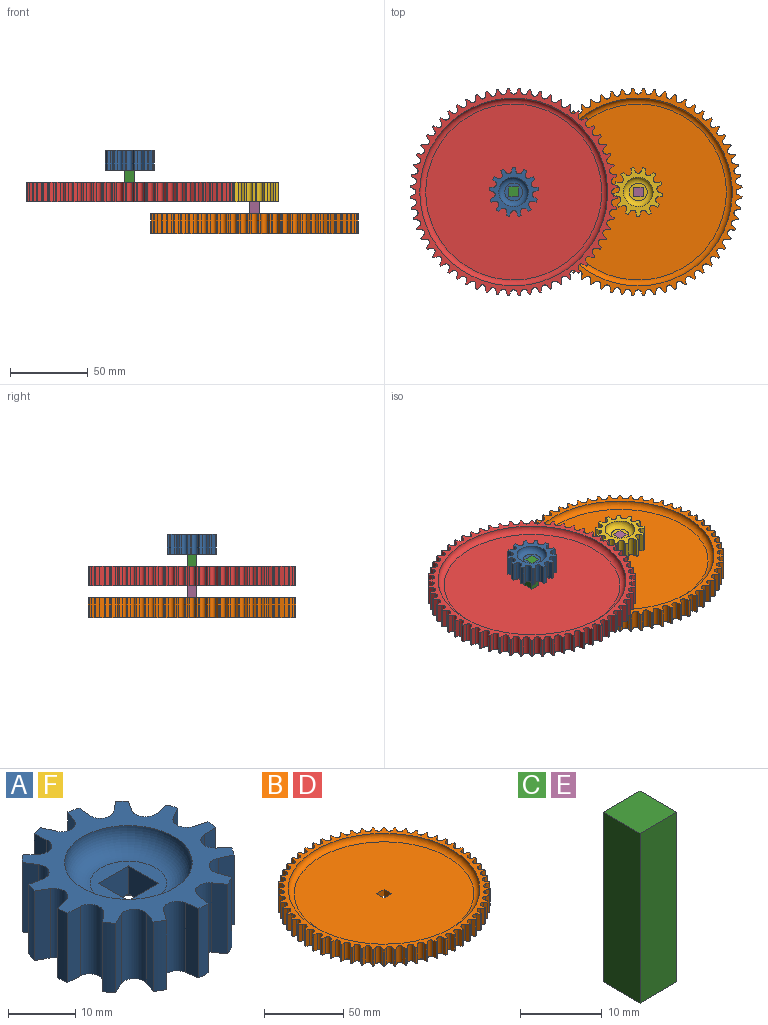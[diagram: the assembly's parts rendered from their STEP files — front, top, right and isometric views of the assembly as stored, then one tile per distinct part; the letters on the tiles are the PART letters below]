
ASSEMBLY  parts=6 mates=5
PART A: 62 faces, bbox 31.7x31.5x15.4 mm
  f0: cylinder r=15.88mm len=12.7mm, axis (0,0,-1), area 24.5mm2, adj f2,f7,f49,f50
  f1: cylinder r=2.06mm len=12.7mm, axis (0,0,-1), area 61.6mm2, adj f2,f3,f49,f50
  f2: plane 12.7x1.9mm, normal (-0.64,0.77,0), area 31.4mm2, adj f0,f1,f49,f50
  f3: plane 12.7x2.46mm, normal (1,-0.09,0), area 31.4mm2, adj f1,f48,f49,f50
  f4: cylinder r=15.88mm len=12.7mm, axis (0,0,-1), area 24.5mm2, adj f6,f11,f49,f50
  f5: cylinder r=2.06mm len=12.7mm, axis (0,0,-1), area 61.6mm2, adj f6,f7,f49,f50
  f6: plane 12.7x2.42mm, normal (-0.21,0.98,0), area 31.4mm2, adj f4,f5,f49,f50
  f7: plane 12.7x2.08mm, normal (0.84,-0.54,0), area 31.4mm2, adj f0,f5,f49,f50
  f8: cylinder r=15.88mm len=12.7mm, axis (0,0,-1), area 24.5mm2, adj f10,f15,f49,f50
  f9: cylinder r=2.06mm len=12.7mm, axis (0,0,-1), area 61.6mm2, adj f10,f11,f49,f50
  f10: plane 12.7x2.38mm, normal (0.27,0.96,0), area 31.4mm2, adj f8,f9,f49,f50
  f11: plane 12.7x2.15mm, normal (0.49,-0.87,0), area 31.4mm2, adj f4,f9,f49,f50
  f12: cylinder r=15.88mm len=12.7mm, axis (0,0,-1), area 24.5mm2, adj f14,f19,f49,f50
  f13: cylinder r=2.06mm len=12.7mm, axis (0,0,-1), area 61.6mm2, adj f14,f15,f49,f50
  f14: plane 12.7x1.8mm, normal (0.69,0.73,0), area 31.4mm2, adj f12,f13,f49,f50
  f15: plane 12.7x2.47mm, normal (0.03,-1,0), area 31.4mm2, adj f8,f13,f49,f50
  f16: cylinder r=15.88mm len=12.7mm, axis (0,0,-1), area 24.5mm2, adj f18,f23,f49,f50
  f17: cylinder r=2.06mm len=12.7mm, axis (0,0,-1), area 61.6mm2, adj f18,f19,f49,f50
  f18: plane 12.7x2.34mm, normal (0.95,0.32,0), area 31.4mm2, adj f16,f17,f49,f50
  f19: plane 12.7x2.22mm, normal (-0.44,-0.9,0), area 31.4mm2, adj f12,f17,f49,f50
  f20: cylinder r=15.88mm len=12.7mm, axis (0,0,-1), area 24.5mm2, adj f22,f27,f49,f50
  f21: cylinder r=2.06mm len=12.7mm, axis (0,0,-1), area 61.6mm2, adj f22,f23,f49,f50
  f22: plane 12.7x2.44mm, normal (0.99,-0.15,0), area 31.4mm2, adj f20,f21,f49,f50
  f23: plane 12.7x1.99mm, normal (-0.8,-0.59,0), area 31.4mm2, adj f16,f21,f49,f50
  f24: cylinder r=15.88mm len=12.7mm, axis (0,0,-1), area 24.5mm2, adj f26,f31,f49,f50
  f25: cylinder r=2.06mm len=12.7mm, axis (0,0,-1), area 61.6mm2, adj f26,f27,f49,f50
  f26: plane 12.7x1.99mm, normal (0.8,-0.59,0), area 31.4mm2, adj f24,f25,f49,f50
  f27: plane 12.7x2.44mm, normal (-0.99,-0.15,0), area 31.4mm2, adj f20,f25,f49,f50
  f28: cylinder r=15.88mm len=12.7mm, axis (0,0,-1), area 24.5mm2, adj f30,f35,f49,f50
  f29: cylinder r=2.06mm len=12.7mm, axis (0,0,-1), area 61.6mm2, adj f30,f31,f49,f50
  f30: plane 12.7x2.22mm, normal (0.44,-0.9,0), area 31.4mm2, adj f28,f29,f49,f50
  f31: plane 12.7x2.34mm, normal (-0.95,0.32,0), area 31.4mm2, adj f24,f29,f49,f50
  f32: cylinder r=15.88mm len=12.7mm, axis (0,0,-1), area 24.5mm2, adj f34,f39,f49,f50
  f33: cylinder r=2.06mm len=12.7mm, axis (0,0,-1), area 61.6mm2, adj f34,f35,f49,f50
  f34: plane 12.7x2.47mm, normal (-0.03,-1,0), area 31.4mm2, adj f32,f33,f49,f50
  f35: plane 12.7x1.8mm, normal (-0.69,0.73,0), area 31.4mm2, adj f28,f33,f49,f50
  f36: cylinder r=15.88mm len=12.7mm, axis (0,0,-1), area 24.5mm2, adj f38,f43,f49,f50
  f37: cylinder r=2.06mm len=12.7mm, axis (0,0,-1), area 61.6mm2, adj f38,f39,f49,f50
  f38: plane 12.7x2.15mm, normal (-0.49,-0.87,0), area 31.4mm2, adj f36,f37,f49,f50
  f39: plane 12.7x2.38mm, normal (-0.27,0.96,0), area 31.4mm2, adj f32,f37,f49,f50
  f40: cylinder r=15.88mm len=12.7mm, axis (0,0,-1), area 24.5mm2, adj f42,f47,f49,f50
  f41: cylinder r=2.06mm len=12.7mm, axis (0,0,-1), area 61.6mm2, adj f42,f43,f49,f50
  f42: plane 12.7x2.08mm, normal (-0.84,-0.54,0), area 31.4mm2, adj f40,f41,f49,f50
  f43: plane 12.7x2.42mm, normal (0.21,0.98,0), area 31.4mm2, adj f36,f41,f49,f50
  f44: cylinder r=15.88mm len=12.7mm, axis (0,0,-1), area 24.5mm2, adj f46,f49,f50,f57
  f45: cylinder r=2.06mm len=12.7mm, axis (0,0,-1), area 61.6mm2, adj f46,f47,f49,f50
  f46: plane 12.7x2.46mm, normal (-1,-0.09,0), area 31.4mm2, adj f44,f45,f49,f50
  f47: plane 12.7x1.9mm, normal (0.64,0.77,0), area 31.4mm2, adj f40,f45,f49,f50
  f48: cylinder r=15.88mm len=12.7mm, axis (0,0,-1), area 24.5mm2, adj f3,f49,f50,f56
  f49: plane 31.69x31.49mm, normal (0,0,-1), area 307.2mm2, adj f0,f1,f2,f3,f4,f5,f6,f7
  f50: plane 31.69x31.49mm, normal (0,0,1), area 307.2mm2, adj f0,f1,f2,f3,f4,f5,f6,f7
  f51: torus R=5.71mm, axis (0,0,-1), area 306.1mm2, adj f49,f54
  f52: torus R=5.71mm, axis (0,0,-1), area 306.1mm2, adj f50,f53
  f53: plane 11.43x11.43mm, normal (0,0,1), area 62.3mm2, adj f52,f58,f59,f60,f61
  f54: plane 11.43x11.43mm, normal (0,0,-1), area 62.3mm2, adj f51,f58,f59,f60,f61
  f55: cylinder r=2.06mm len=12.7mm, axis (0,0,-1), area 61.6mm2, adj f49,f50,f56,f57
  f56: plane 12.7x2.28mm, normal (-0.92,0.38,0), area 31.4mm2, adj f48,f49,f50,f55
  f57: plane 12.7x2.28mm, normal (0.92,0.38,0), area 31.4mm2, adj f44,f49,f50,f55
  f58: plane 6.35x5.08mm, normal (-1,0,0), area 32.3mm2, adj f53,f54,f59,f61
  f59: plane 6.35x5.08mm, normal (0,-1,0), area 32.3mm2, adj f53,f54,f58,f60
  f60: plane 6.35x5.08mm, normal (1,0,0), area 32.3mm2, adj f53,f54,f59,f61
  f61: plane 6.35x5.08mm, normal (0,1,0), area 32.3mm2, adj f53,f54,f58,f60
PART B: 250 faces, bbox 133.2x133.2x15.4 mm
  f0: plane 113.03x113.03mm, normal (0,0,1), area 9993.8mm2, adj f239,f246,f247,f248,f249
  f1: plane 113.03x113.03mm, normal (0,0,-1), area 9993.8mm2, adj f240,f246,f247,f248,f249
  f2: cylinder r=66.67mm len=12.7mm, axis (0,0,-1), area 14.1mm2, adj f4,f9,f241,f242
  f3: cylinder r=2.06mm len=12.7mm, axis (0,0,1), area 61.6mm2, adj f4,f5,f241,f242
  f4: plane 12.7x2.35mm, normal (-0.88,0.48,0), area 34.1mm2, adj f2,f3,f241,f242
  f5: plane 12.7x2.57mm, normal (0.96,0.29,0), area 34.1mm2, adj f3,f238,f241,f242
  f6: cylinder r=66.67mm len=12.7mm, axis (0,0,-1), area 14.1mm2, adj f8,f13,f241,f242
  f7: cylinder r=2.06mm len=12.7mm, axis (0,0,1), area 61.6mm2, adj f8,f9,f241,f242
  f8: plane 12.7x2.21mm, normal (-0.82,0.57,0), area 34.1mm2, adj f6,f7,f241,f242
  f9: plane 12.7x2.64mm, normal (0.98,0.18,0), area 34.1mm2, adj f2,f7,f241,f242
  f10: cylinder r=66.67mm len=12.7mm, axis (0,0,-1), area 14.1mm2, adj f12,f17,f241,f242
  f11: cylinder r=2.06mm len=12.7mm, axis (0,0,1), area 61.6mm2, adj f12,f13,f241,f242
  f12: plane 12.7x2.04mm, normal (-0.76,0.65,0), area 34.1mm2, adj f10,f11,f241,f242
  f13: plane 12.7x2.67mm, normal (1,0.08,0), area 34.1mm2, adj f6,f11,f241,f242
  f14: cylinder r=66.67mm len=12.7mm, axis (0,0,-1), area 14.1mm2, adj f16,f21,f241,f242
  f15: cylinder r=2.06mm len=12.7mm, axis (0,0,1), area 61.6mm2, adj f16,f17,f241,f242
  f16: plane 12.7x1.95mm, normal (-0.69,0.73,0), area 34.1mm2, adj f14,f15,f241,f242
  f17: plane 12.7x2.68mm, normal (1,-0.02,0), area 34.1mm2, adj f10,f15,f241,f242
  f18: cylinder r=66.67mm len=12.7mm, axis (0,0,-1), area 14.1mm2, adj f20,f25,f241,f242
  f19: cylinder r=2.06mm len=12.7mm, axis (0,0,1), area 61.6mm2, adj f20,f21,f241,f242
  f20: plane 12.7x2.13mm, normal (-0.61,0.79,0), area 34.1mm2, adj f18,f19,f241,f242
  f21: plane 12.7x2.66mm, normal (0.99,-0.13,0), area 34.1mm2, adj f14,f19,f241,f242
  f22: cylinder r=66.67mm len=12.7mm, axis (0,0,-1), area 14.1mm2, adj f24,f29,f241,f242
  f23: cylinder r=2.06mm len=12.7mm, axis (0,0,1), area 61.6mm2, adj f24,f25,f241,f242
  f24: plane 12.7x2.29mm, normal (-0.52,0.85,0), area 34.1mm2, adj f22,f23,f241,f242
  f25: plane 12.7x2.61mm, normal (0.97,-0.23,0), area 34.1mm2, adj f18,f23,f241,f242
  f26: cylinder r=66.67mm len=12.7mm, axis (0,0,-1), area 14.1mm2, adj f28,f33,f241,f242
  f27: cylinder r=2.06mm len=12.7mm, axis (0,0,1), area 61.6mm2, adj f28,f29,f241,f242
  f28: plane 12.7x2.42mm, normal (-0.43,0.9,0), area 34.1mm2, adj f26,f27,f241,f242
  f29: plane 12.7x2.53mm, normal (0.94,-0.33,0), area 34.1mm2, adj f22,f27,f241,f242
  f30: cylinder r=66.67mm len=12.7mm, axis (0,0,-1), area 14.1mm2, adj f32,f37,f241,f242
  f31: cylinder r=2.06mm len=12.7mm, axis (0,0,1), area 61.6mm2, adj f32,f33,f241,f242
  f32: plane 12.7x2.53mm, normal (-0.33,0.94,0), area 34.1mm2, adj f30,f31,f241,f242
  f33: plane 12.7x2.42mm, normal (0.9,-0.43,0), area 34.1mm2, adj f26,f31,f241,f242
  f34: cylinder r=66.67mm len=12.7mm, axis (0,0,-1), area 14.1mm2, adj f36,f41,f241,f242
  f35: cylinder r=2.06mm len=12.7mm, axis (0,0,1), area 61.6mm2, adj f36,f37,f241,f242
  f36: plane 12.7x2.61mm, normal (-0.23,0.97,0), area 34.1mm2, adj f34,f35,f241,f242
  f37: plane 12.7x2.29mm, normal (0.85,-0.52,0), area 34.1mm2, adj f30,f35,f241,f242
  f38: cylinder r=66.67mm len=12.7mm, axis (0,0,-1), area 14.1mm2, adj f40,f45,f241,f242
  f39: cylinder r=2.06mm len=12.7mm, axis (0,0,1), area 61.6mm2, adj f40,f41,f241,f242
  f40: plane 12.7x2.66mm, normal (-0.13,0.99,0), area 34.1mm2, adj f38,f39,f241,f242
  f41: plane 12.7x2.13mm, normal (0.79,-0.61,0), area 34.1mm2, adj f34,f39,f241,f242
  f42: cylinder r=66.67mm len=12.7mm, axis (0,0,-1), area 14.1mm2, adj f44,f49,f241,f242
  f43: cylinder r=2.06mm len=12.7mm, axis (0,0,1), area 61.6mm2, adj f44,f45,f241,f242
  f44: plane 12.7x2.68mm, normal (-0.02,1,0), area 34.1mm2, adj f42,f43,f241,f242
  f45: plane 12.7x1.95mm, normal (0.73,-0.69,0), area 34.1mm2, adj f38,f43,f241,f242
  f46: cylinder r=66.67mm len=12.7mm, axis (0,0,-1), area 14.1mm2, adj f48,f53,f241,f242
  f47: cylinder r=2.06mm len=12.7mm, axis (0,0,1), area 61.6mm2, adj f48,f49,f241,f242
  f48: plane 12.7x2.67mm, normal (0.08,1,0), area 34.1mm2, adj f46,f47,f241,f242
  f49: plane 12.7x2.04mm, normal (0.65,-0.76,0), area 34.1mm2, adj f42,f47,f241,f242
  f50: cylinder r=66.67mm len=12.7mm, axis (0,0,-1), area 14.1mm2, adj f52,f57,f241,f242
  f51: cylinder r=2.06mm len=12.7mm, axis (0,0,1), area 61.6mm2, adj f52,f53,f241,f242
  f52: plane 12.7x2.64mm, normal (0.18,0.98,0), area 34.1mm2, adj f50,f51,f241,f242
  f53: plane 12.7x2.21mm, normal (0.57,-0.82,0), area 34.1mm2, adj f46,f51,f241,f242
  f54: cylinder r=66.67mm len=12.7mm, axis (0,0,-1), area 14.1mm2, adj f56,f61,f241,f242
  f55: cylinder r=2.06mm len=12.7mm, axis (0,0,1), area 61.6mm2, adj f56,f57,f241,f242
  f56: plane 12.7x2.57mm, normal (0.29,0.96,0), area 34.1mm2, adj f54,f55,f241,f242
  f57: plane 12.7x2.35mm, normal (0.48,-0.88,0), area 34.1mm2, adj f50,f55,f241,f242
  f58: cylinder r=66.67mm len=12.7mm, axis (0,0,-1), area 14.1mm2, adj f60,f65,f241,f242
  f59: cylinder r=2.06mm len=12.7mm, axis (0,0,1), area 61.6mm2, adj f60,f61,f241,f242
  f60: plane 12.7x2.48mm, normal (0.38,0.92,0), area 34.1mm2, adj f58,f59,f241,f242
  f61: plane 12.7x2.48mm, normal (0.38,-0.92,0), area 34.1mm2, adj f54,f59,f241,f242
  f62: cylinder r=66.67mm len=12.7mm, axis (0,0,-1), area 14.1mm2, adj f64,f69,f241,f242
  f63: cylinder r=2.06mm len=12.7mm, axis (0,0,1), area 61.6mm2, adj f64,f65,f241,f242
  f64: plane 12.7x2.35mm, normal (0.48,0.88,0), area 34.1mm2, adj f62,f63,f241,f242
  f65: plane 12.7x2.57mm, normal (0.29,-0.96,0), area 34.1mm2, adj f58,f63,f241,f242
  f66: cylinder r=66.67mm len=12.7mm, axis (0,0,-1), area 14.1mm2, adj f68,f73,f241,f242
  f67: cylinder r=2.06mm len=12.7mm, axis (0,0,1), area 61.6mm2, adj f68,f69,f241,f242
  f68: plane 12.7x2.21mm, normal (0.57,0.82,0), area 34.1mm2, adj f66,f67,f241,f242
  f69: plane 12.7x2.64mm, normal (0.18,-0.98,0), area 34.1mm2, adj f62,f67,f241,f242
  f70: cylinder r=66.67mm len=12.7mm, axis (0,0,-1), area 14.1mm2, adj f72,f77,f241,f242
  f71: cylinder r=2.06mm len=12.7mm, axis (0,0,1), area 61.6mm2, adj f72,f73,f241,f242
  f72: plane 12.7x2.04mm, normal (0.65,0.76,0), area 34.1mm2, adj f70,f71,f241,f242
  f73: plane 12.7x2.67mm, normal (0.08,-1,0), area 34.1mm2, adj f66,f71,f241,f242
  f74: cylinder r=66.67mm len=12.7mm, axis (0,0,-1), area 14.1mm2, adj f76,f81,f241,f242
  f75: cylinder r=2.06mm len=12.7mm, axis (0,0,1), area 61.6mm2, adj f76,f77,f241,f242
  f76: plane 12.7x1.95mm, normal (0.73,0.69,0), area 34.1mm2, adj f74,f75,f241,f242
  f77: plane 12.7x2.68mm, normal (-0.02,-1,0), area 34.1mm2, adj f70,f75,f241,f242
  f78: cylinder r=66.67mm len=12.7mm, axis (0,0,-1), area 14.1mm2, adj f80,f85,f241,f242
  f79: cylinder r=2.06mm len=12.7mm, axis (0,0,1), area 61.6mm2, adj f80,f81,f241,f242
  f80: plane 12.7x2.13mm, normal (0.79,0.61,0), area 34.1mm2, adj f78,f79,f241,f242
  f81: plane 12.7x2.66mm, normal (-0.13,-0.99,0), area 34.1mm2, adj f74,f79,f241,f242
  f82: cylinder r=66.67mm len=12.7mm, axis (0,0,-1), area 14.1mm2, adj f84,f89,f241,f242
  f83: cylinder r=2.06mm len=12.7mm, axis (0,0,1), area 61.6mm2, adj f84,f85,f241,f242
  f84: plane 12.7x2.29mm, normal (0.85,0.52,0), area 34.1mm2, adj f82,f83,f241,f242
  f85: plane 12.7x2.61mm, normal (-0.23,-0.97,0), area 34.1mm2, adj f78,f83,f241,f242
  f86: cylinder r=66.67mm len=12.7mm, axis (0,0,-1), area 14.1mm2, adj f88,f93,f241,f242
  f87: cylinder r=2.06mm len=12.7mm, axis (0,0,1), area 61.6mm2, adj f88,f89,f241,f242
  f88: plane 12.7x2.42mm, normal (0.9,0.43,0), area 34.1mm2, adj f86,f87,f241,f242
  f89: plane 12.7x2.53mm, normal (-0.33,-0.94,0), area 34.1mm2, adj f82,f87,f241,f242
  f90: cylinder r=66.67mm len=12.7mm, axis (0,0,-1), area 14.1mm2, adj f92,f97,f241,f242
  f91: cylinder r=2.06mm len=12.7mm, axis (0,0,1), area 61.6mm2, adj f92,f93,f241,f242
  f92: plane 12.7x2.53mm, normal (0.94,0.33,0), area 34.1mm2, adj f90,f91,f241,f242
  f93: plane 12.7x2.42mm, normal (-0.43,-0.9,0), area 34.1mm2, adj f86,f91,f241,f242
  f94: cylinder r=66.67mm len=12.7mm, axis (0,0,-1), area 14.1mm2, adj f96,f101,f241,f242
  f95: cylinder r=2.06mm len=12.7mm, axis (0,0,1), area 61.6mm2, adj f96,f97,f241,f242
  f96: plane 12.7x2.61mm, normal (0.97,0.23,0), area 34.1mm2, adj f94,f95,f241,f242
  f97: plane 12.7x2.29mm, normal (-0.52,-0.85,0), area 34.1mm2, adj f90,f95,f241,f242
  f98: cylinder r=66.67mm len=12.7mm, axis (0,0,-1), area 14.1mm2, adj f100,f105,f241,f242
  f99: cylinder r=2.06mm len=12.7mm, axis (0,0,1), area 61.6mm2, adj f100,f101,f241,f242
  f100: plane 12.7x2.66mm, normal (0.99,0.13,0), area 34.1mm2, adj f98,f99,f241,f242
  f101: plane 12.7x2.13mm, normal (-0.61,-0.79,0), area 34.1mm2, adj f94,f99,f241,f242
  f102: cylinder r=66.67mm len=12.7mm, axis (0,0,-1), area 14.1mm2, adj f104,f109,f241,f242
  f103: cylinder r=2.06mm len=12.7mm, axis (0,0,1), area 61.6mm2, adj f104,f105,f241,f242
  f104: plane 12.7x2.68mm, normal (1,0.02,0), area 34.1mm2, adj f102,f103,f241,f242
  f105: plane 12.7x1.95mm, normal (-0.69,-0.73,0), area 34.1mm2, adj f98,f103,f241,f242
  f106: cylinder r=66.67mm len=12.7mm, axis (0,0,-1), area 14.1mm2, adj f108,f113,f241,f242
  f107: cylinder r=2.06mm len=12.7mm, axis (0,0,1), area 61.6mm2, adj f108,f109,f241,f242
  f108: plane 12.7x2.67mm, normal (1,-0.08,0), area 34.1mm2, adj f106,f107,f241,f242
  f109: plane 12.7x2.04mm, normal (-0.76,-0.65,0), area 34.1mm2, adj f102,f107,f241,f242
  f110: cylinder r=66.67mm len=12.7mm, axis (0,0,-1), area 14.1mm2, adj f112,f117,f241,f242
  f111: cylinder r=2.06mm len=12.7mm, axis (0,0,1), area 61.6mm2, adj f112,f113,f241,f242
  f112: plane 12.7x2.64mm, normal (0.98,-0.18,0), area 34.1mm2, adj f110,f111,f241,f242
  f113: plane 12.7x2.21mm, normal (-0.82,-0.57,0), area 34.1mm2, adj f106,f111,f241,f242
  f114: cylinder r=66.67mm len=12.7mm, axis (0,0,-1), area 14.1mm2, adj f116,f121,f241,f242
  f115: cylinder r=2.06mm len=12.7mm, axis (0,0,1), area 61.6mm2, adj f116,f117,f241,f242
  f116: plane 12.7x2.57mm, normal (0.96,-0.29,0), area 34.1mm2, adj f114,f115,f241,f242
  f117: plane 12.7x2.35mm, normal (-0.88,-0.48,0), area 34.1mm2, adj f110,f115,f241,f242
  f118: cylinder r=66.67mm len=12.7mm, axis (0,0,-1), area 14.1mm2, adj f120,f125,f241,f242
  f119: cylinder r=2.06mm len=12.7mm, axis (0,0,1), area 61.6mm2, adj f120,f121,f241,f242
  f120: plane 12.7x2.48mm, normal (0.92,-0.38,0), area 34.1mm2, adj f118,f119,f241,f242
  f121: plane 12.7x2.48mm, normal (-0.92,-0.38,0), area 34.1mm2, adj f114,f119,f241,f242
  f122: cylinder r=66.67mm len=12.7mm, axis (0,0,-1), area 14.1mm2, adj f124,f129,f241,f242
  f123: cylinder r=2.06mm len=12.7mm, axis (0,0,1), area 61.6mm2, adj f124,f125,f241,f242
  f124: plane 12.7x2.35mm, normal (0.88,-0.48,0), area 34.1mm2, adj f122,f123,f241,f242
  f125: plane 12.7x2.57mm, normal (-0.96,-0.29,0), area 34.1mm2, adj f118,f123,f241,f242
  f126: cylinder r=66.67mm len=12.7mm, axis (0,0,-1), area 14.1mm2, adj f128,f133,f241,f242
  f127: cylinder r=2.06mm len=12.7mm, axis (0,0,1), area 61.6mm2, adj f128,f129,f241,f242
  f128: plane 12.7x2.21mm, normal (0.82,-0.57,0), area 34.1mm2, adj f126,f127,f241,f242
  f129: plane 12.7x2.64mm, normal (-0.98,-0.18,0), area 34.1mm2, adj f122,f127,f241,f242
  f130: cylinder r=66.67mm len=12.7mm, axis (0,0,-1), area 14.1mm2, adj f132,f137,f241,f242
  f131: cylinder r=2.06mm len=12.7mm, axis (0,0,1), area 61.6mm2, adj f132,f133,f241,f242
  f132: plane 12.7x2.04mm, normal (0.76,-0.65,0), area 34.1mm2, adj f130,f131,f241,f242
  f133: plane 12.7x2.67mm, normal (-1,-0.08,0), area 34.1mm2, adj f126,f131,f241,f242
  f134: cylinder r=66.67mm len=12.7mm, axis (0,0,-1), area 14.1mm2, adj f136,f141,f241,f242
  f135: cylinder r=2.06mm len=12.7mm, axis (0,0,1), area 61.6mm2, adj f136,f137,f241,f242
  f136: plane 12.7x1.95mm, normal (0.69,-0.73,0), area 34.1mm2, adj f134,f135,f241,f242
  f137: plane 12.7x2.68mm, normal (-1,0.02,0), area 34.1mm2, adj f130,f135,f241,f242
  f138: cylinder r=66.67mm len=12.7mm, axis (0,0,-1), area 14.1mm2, adj f140,f145,f241,f242
  f139: cylinder r=2.06mm len=12.7mm, axis (0,0,1), area 61.6mm2, adj f140,f141,f241,f242
  f140: plane 12.7x2.13mm, normal (0.61,-0.79,0), area 34.1mm2, adj f138,f139,f241,f242
  f141: plane 12.7x2.66mm, normal (-0.99,0.13,0), area 34.1mm2, adj f134,f139,f241,f242
  f142: cylinder r=66.67mm len=12.7mm, axis (0,0,-1), area 14.1mm2, adj f144,f149,f241,f242
  f143: cylinder r=2.06mm len=12.7mm, axis (0,0,1), area 61.6mm2, adj f144,f145,f241,f242
  f144: plane 12.7x2.29mm, normal (0.52,-0.85,0), area 34.1mm2, adj f142,f143,f241,f242
  f145: plane 12.7x2.61mm, normal (-0.97,0.23,0), area 34.1mm2, adj f138,f143,f241,f242
  f146: cylinder r=66.67mm len=12.7mm, axis (0,0,-1), area 14.1mm2, adj f148,f153,f241,f242
  f147: cylinder r=2.06mm len=12.7mm, axis (0,0,1), area 61.6mm2, adj f148,f149,f241,f242
  f148: plane 12.7x2.42mm, normal (0.43,-0.9,0), area 34.1mm2, adj f146,f147,f241,f242
  f149: plane 12.7x2.53mm, normal (-0.94,0.33,0), area 34.1mm2, adj f142,f147,f241,f242
  f150: cylinder r=66.67mm len=12.7mm, axis (0,0,-1), area 14.1mm2, adj f152,f157,f241,f242
  f151: cylinder r=2.06mm len=12.7mm, axis (0,0,1), area 61.6mm2, adj f152,f153,f241,f242
  f152: plane 12.7x2.53mm, normal (0.33,-0.94,0), area 34.1mm2, adj f150,f151,f241,f242
  f153: plane 12.7x2.42mm, normal (-0.9,0.43,0), area 34.1mm2, adj f146,f151,f241,f242
  f154: cylinder r=66.67mm len=12.7mm, axis (0,0,-1), area 14.1mm2, adj f156,f161,f241,f242
  f155: cylinder r=2.06mm len=12.7mm, axis (0,0,1), area 61.6mm2, adj f156,f157,f241,f242
  f156: plane 12.7x2.61mm, normal (0.23,-0.97,0), area 34.1mm2, adj f154,f155,f241,f242
  f157: plane 12.7x2.29mm, normal (-0.85,0.52,0), area 34.1mm2, adj f150,f155,f241,f242
  f158: cylinder r=66.67mm len=12.7mm, axis (0,0,-1), area 14.1mm2, adj f160,f165,f241,f242
  f159: cylinder r=2.06mm len=12.7mm, axis (0,0,1), area 61.6mm2, adj f160,f161,f241,f242
  f160: plane 12.7x2.66mm, normal (0.13,-0.99,0), area 34.1mm2, adj f158,f159,f241,f242
  f161: plane 12.7x2.13mm, normal (-0.79,0.61,0), area 34.1mm2, adj f154,f159,f241,f242
  f162: cylinder r=66.67mm len=12.7mm, axis (0,0,-1), area 14.1mm2, adj f164,f169,f241,f242
  f163: cylinder r=2.06mm len=12.7mm, axis (0,0,1), area 61.6mm2, adj f164,f165,f241,f242
  f164: plane 12.7x2.68mm, normal (0.02,-1,0), area 34.1mm2, adj f162,f163,f241,f242
  f165: plane 12.7x1.95mm, normal (-0.73,0.69,0), area 34.1mm2, adj f158,f163,f241,f242
  f166: cylinder r=66.67mm len=12.7mm, axis (0,0,-1), area 14.1mm2, adj f168,f173,f241,f242
  f167: cylinder r=2.06mm len=12.7mm, axis (0,0,1), area 61.6mm2, adj f168,f169,f241,f242
  f168: plane 12.7x2.67mm, normal (-0.08,-1,0), area 34.1mm2, adj f166,f167,f241,f242
  f169: plane 12.7x2.04mm, normal (-0.65,0.76,0), area 34.1mm2, adj f162,f167,f241,f242
  f170: cylinder r=66.67mm len=12.7mm, axis (0,0,-1), area 14.1mm2, adj f172,f177,f241,f242
  f171: cylinder r=2.06mm len=12.7mm, axis (0,0,1), area 61.6mm2, adj f172,f173,f241,f242
  f172: plane 12.7x2.64mm, normal (-0.18,-0.98,0), area 34.1mm2, adj f170,f171,f241,f242
  f173: plane 12.7x2.21mm, normal (-0.57,0.82,0), area 34.1mm2, adj f166,f171,f241,f242
  f174: cylinder r=66.67mm len=12.7mm, axis (0,0,-1), area 14.1mm2, adj f176,f181,f241,f242
  f175: cylinder r=2.06mm len=12.7mm, axis (0,0,1), area 61.6mm2, adj f176,f177,f241,f242
  f176: plane 12.7x2.57mm, normal (-0.29,-0.96,0), area 34.1mm2, adj f174,f175,f241,f242
  f177: plane 12.7x2.35mm, normal (-0.48,0.88,0), area 34.1mm2, adj f170,f175,f241,f242
  f178: cylinder r=66.67mm len=12.7mm, axis (0,0,-1), area 14.1mm2, adj f180,f185,f241,f242
  f179: cylinder r=2.06mm len=12.7mm, axis (0,0,1), area 61.6mm2, adj f180,f181,f241,f242
  f180: plane 12.7x2.48mm, normal (-0.38,-0.92,0), area 34.1mm2, adj f178,f179,f241,f242
  f181: plane 12.7x2.48mm, normal (-0.38,0.92,0), area 34.1mm2, adj f174,f179,f241,f242
  f182: cylinder r=66.67mm len=12.7mm, axis (0,0,-1), area 14.1mm2, adj f184,f189,f241,f242
  f183: cylinder r=2.06mm len=12.7mm, axis (0,0,1), area 61.6mm2, adj f184,f185,f241,f242
  f184: plane 12.7x2.35mm, normal (-0.48,-0.88,0), area 34.1mm2, adj f182,f183,f241,f242
  f185: plane 12.7x2.57mm, normal (-0.29,0.96,0), area 34.1mm2, adj f178,f183,f241,f242
  f186: cylinder r=66.67mm len=12.7mm, axis (0,0,-1), area 14.1mm2, adj f188,f193,f241,f242
  f187: cylinder r=2.06mm len=12.7mm, axis (0,0,1), area 61.6mm2, adj f188,f189,f241,f242
  f188: plane 12.7x2.21mm, normal (-0.57,-0.82,0), area 34.1mm2, adj f186,f187,f241,f242
  f189: plane 12.7x2.64mm, normal (-0.18,0.98,0), area 34.1mm2, adj f182,f187,f241,f242
  f190: cylinder r=66.67mm len=12.7mm, axis (0,0,-1), area 14.1mm2, adj f192,f197,f241,f242
  f191: cylinder r=2.06mm len=12.7mm, axis (0,0,1), area 61.6mm2, adj f192,f193,f241,f242
  f192: plane 12.7x2.04mm, normal (-0.65,-0.76,0), area 34.1mm2, adj f190,f191,f241,f242
  f193: plane 12.7x2.67mm, normal (-0.08,1,0), area 34.1mm2, adj f186,f191,f241,f242
  f194: cylinder r=66.67mm len=12.7mm, axis (0,0,-1), area 14.1mm2, adj f196,f201,f241,f242
  f195: cylinder r=2.06mm len=12.7mm, axis (0,0,1), area 61.6mm2, adj f196,f197,f241,f242
  f196: plane 12.7x1.95mm, normal (-0.73,-0.69,0), area 34.1mm2, adj f194,f195,f241,f242
  f197: plane 12.7x2.68mm, normal (0.02,1,0), area 34.1mm2, adj f190,f195,f241,f242
  f198: cylinder r=66.67mm len=12.7mm, axis (0,0,-1), area 14.1mm2, adj f200,f205,f241,f242
  f199: cylinder r=2.06mm len=12.7mm, axis (0,0,1), area 61.6mm2, adj f200,f201,f241,f242
  f200: plane 12.7x2.13mm, normal (-0.79,-0.61,0), area 34.1mm2, adj f198,f199,f241,f242
  f201: plane 12.7x2.66mm, normal (0.13,0.99,0), area 34.1mm2, adj f194,f199,f241,f242
  f202: cylinder r=66.67mm len=12.7mm, axis (0,0,-1), area 14.1mm2, adj f204,f209,f241,f242
  f203: cylinder r=2.06mm len=12.7mm, axis (0,0,1), area 61.6mm2, adj f204,f205,f241,f242
  f204: plane 12.7x2.29mm, normal (-0.85,-0.52,0), area 34.1mm2, adj f202,f203,f241,f242
  f205: plane 12.7x2.61mm, normal (0.23,0.97,0), area 34.1mm2, adj f198,f203,f241,f242
  f206: cylinder r=66.67mm len=12.7mm, axis (0,0,-1), area 14.1mm2, adj f208,f213,f241,f242
  f207: cylinder r=2.06mm len=12.7mm, axis (0,0,1), area 61.6mm2, adj f208,f209,f241,f242
  f208: plane 12.7x2.42mm, normal (-0.9,-0.43,0), area 34.1mm2, adj f206,f207,f241,f242
  f209: plane 12.7x2.53mm, normal (0.33,0.94,0), area 34.1mm2, adj f202,f207,f241,f242
  f210: cylinder r=66.67mm len=12.7mm, axis (0,0,-1), area 14.1mm2, adj f212,f217,f241,f242
  f211: cylinder r=2.06mm len=12.7mm, axis (0,0,1), area 61.6mm2, adj f212,f213,f241,f242
  f212: plane 12.7x2.53mm, normal (-0.94,-0.33,0), area 34.1mm2, adj f210,f211,f241,f242
  f213: plane 12.7x2.42mm, normal (0.43,0.9,0), area 34.1mm2, adj f206,f211,f241,f242
  f214: cylinder r=66.67mm len=12.7mm, axis (0,0,-1), area 14.1mm2, adj f216,f221,f241,f242
  f215: cylinder r=2.06mm len=12.7mm, axis (0,0,1), area 61.6mm2, adj f216,f217,f241,f242
  f216: plane 12.7x2.61mm, normal (-0.97,-0.23,0), area 34.1mm2, adj f214,f215,f241,f242
  f217: plane 12.7x2.29mm, normal (0.52,0.85,0), area 34.1mm2, adj f210,f215,f241,f242
  f218: cylinder r=66.67mm len=12.7mm, axis (0,0,-1), area 14.1mm2, adj f220,f225,f241,f242
  f219: cylinder r=2.06mm len=12.7mm, axis (0,0,1), area 61.6mm2, adj f220,f221,f241,f242
  f220: plane 12.7x2.66mm, normal (-0.99,-0.13,0), area 34.1mm2, adj f218,f219,f241,f242
  f221: plane 12.7x2.13mm, normal (0.61,0.79,0), area 34.1mm2, adj f214,f219,f241,f242
  f222: cylinder r=66.67mm len=12.7mm, axis (0,0,-1), area 14.1mm2, adj f224,f229,f241,f242
  f223: cylinder r=2.06mm len=12.7mm, axis (0,0,1), area 61.6mm2, adj f224,f225,f241,f242
  f224: plane 12.7x2.68mm, normal (-1,-0.02,0), area 34.1mm2, adj f222,f223,f241,f242
  f225: plane 12.7x1.95mm, normal (0.69,0.73,0), area 34.1mm2, adj f218,f223,f241,f242
  f226: cylinder r=66.67mm len=12.7mm, axis (0,0,-1), area 14.1mm2, adj f228,f233,f241,f242
  f227: cylinder r=2.06mm len=12.7mm, axis (0,0,1), area 61.6mm2, adj f228,f229,f241,f242
  f228: plane 12.7x2.67mm, normal (-1,0.08,0), area 34.1mm2, adj f226,f227,f241,f242
  f229: plane 12.7x2.04mm, normal (0.76,0.65,0), area 34.1mm2, adj f222,f227,f241,f242
  f230: cylinder r=66.67mm len=12.7mm, axis (0,0,-1), area 14.1mm2, adj f232,f237,f241,f242
  f231: cylinder r=2.06mm len=12.7mm, axis (0,0,1), area 61.6mm2, adj f232,f233,f241,f242
  f232: plane 12.7x2.64mm, normal (-0.98,0.18,0), area 34.1mm2, adj f230,f231,f241,f242
  f233: plane 12.7x2.21mm, normal (0.82,0.57,0), area 34.1mm2, adj f226,f231,f241,f242
  f234: cylinder r=66.67mm len=12.7mm, axis (0,0,-1), area 14.1mm2, adj f236,f241,f242,f245
  f235: cylinder r=2.06mm len=12.7mm, axis (0,0,1), area 61.6mm2, adj f236,f237,f241,f242
  f236: plane 12.7x2.57mm, normal (-0.96,0.29,0), area 34.1mm2, adj f234,f235,f241,f242
  f237: plane 12.7x2.35mm, normal (0.88,0.48,0), area 34.1mm2, adj f230,f235,f241,f242
  f238: cylinder r=66.67mm len=12.7mm, axis (0,0,-1), area 14.1mm2, adj f5,f241,f242,f244
  f239: torus R=56.52mm, axis (0,0,-1), area 2216.4mm2, adj f0,f242
  f240: torus R=56.52mm, axis (0,0,-1), area 2216.4mm2, adj f1,f241
  f241: plane 133.22x133.22mm, normal (0,0,-1), area 1589.5mm2, adj f2,f3,f4,f5,f6,f7,f8,f9
  f242: plane 133.22x133.22mm, normal (0,0,1), area 1589.5mm2, adj f2,f3,f4,f5,f6,f7,f8,f9
  f243: cylinder r=2.06mm len=12.7mm, axis (0,0,1), area 61.6mm2, adj f241,f242,f244,f245
  f244: plane 12.7x2.48mm, normal (-0.92,0.38,0), area 34.1mm2, adj f238,f241,f242,f243
  f245: plane 12.7x2.48mm, normal (0.92,0.38,0), area 34.1mm2, adj f234,f241,f242,f243
  f246: plane 6.35x5.08mm, normal (0,-1,0), area 32.3mm2, adj f0,f1,f247,f249
  f247: plane 6.35x5.08mm, normal (1,0,0), area 32.3mm2, adj f0,f1,f246,f248
  f248: plane 6.35x5.08mm, normal (0,1,0), area 32.3mm2, adj f0,f1,f247,f249
  f249: plane 6.35x5.08mm, normal (-1,0,0), area 32.3mm2, adj f0,f1,f246,f248
PART C: 6 faces, bbox 6.4x6.4x25.4 mm
  f0: plane 25.4x6.35mm, normal (0,1,0), area 161.3mm2, adj f1,f3,f4,f5
  f1: plane 25.4x6.35mm, normal (-1,0,0), area 161.3mm2, adj f0,f2,f4,f5
  f2: plane 25.4x6.35mm, normal (0,-1,0), area 161.3mm2, adj f1,f3,f4,f5
  f3: plane 25.4x6.35mm, normal (1,0,0), area 161.3mm2, adj f0,f2,f4,f5
  f4: plane 6.35x6.35mm, normal (0,0,1), area 40.3mm2, adj f0,f1,f2,f3
  f5: plane 6.35x6.35mm, normal (0,0,-1), area 40.3mm2, adj f0,f1,f2,f3
PART D: same geometry as B
PART E: same geometry as C
PART F: same geometry as A
PLACE A rot(axis=(1,0,0),180deg) t=(0,0,22.86)mm
PLACE B t=(80.01,0,-17.78)mm
PLACE C rot(axis=(-0.37,-0.92,0.1),0deg) t=(0,0,12.7)mm
PLACE D rot(axis=(-0.37,-0.92,0.1),0deg) t=(0,0,2.54)mm
PLACE E t=(80.01,0,-7.62)mm
PLACE F t=(80.01,0,2.54)mm
MATE fastened E.f4 <-> F.f0  axis (0,0,1) through (80.01,0,5.08)mm
MATE fastened E.f5 <-> B.f2  axis (0,0,-1) through (80.01,0,-20.32)mm
MATE revolute E.f5 <-> B.f2  axis (0,0,-1) through (80.01,0,-20.32)mm
MATE fastened C.f5 <-> D.f2  axis (0,0,-1) through (0,0,0)mm
MATE fastened A.f0 <-> C.f4  axis (0,0,1) through (0,0,25.4)mm
